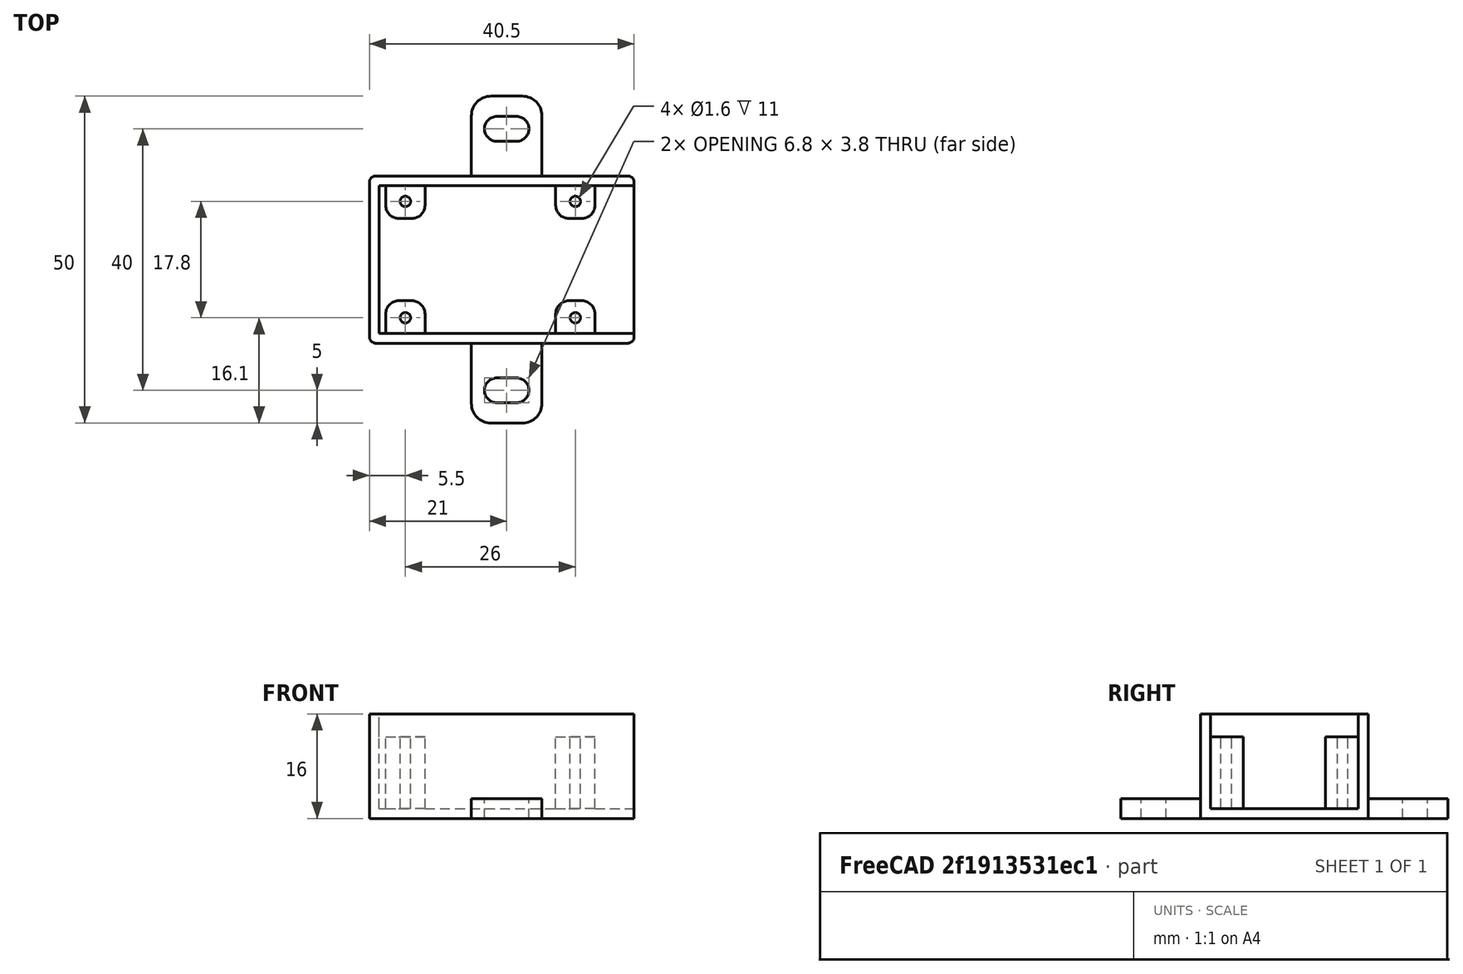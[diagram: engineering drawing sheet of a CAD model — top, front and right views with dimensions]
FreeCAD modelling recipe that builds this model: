
FCSTD DOCUMENT  (FreeCAD 0.18.4R)
Label: ds3231sn_clock
License: FreeArt
LicenseURL: http://artlibre.org/licence/lal
objects: Part::Box×4, Part::MultiFuse×4, Part::Fillet×2, Part::Cut×2, Spreadsheet::Sheet×1, Part::Cylinder×1, Part::FeaturePython×1, Part::Mirroring×1, Part::Feature×1, App::Part×1
note: 16 computed .brp shape members not serialized (recipe doc carries the construction recipe); baked Part::Feature solids carry a one-line shape summary decoded from their .brp

FEATURE [Spreadsheet::Sheet] Spreadsheet  label="p"
  cells = A1=pcb_x; B1(pcb_x)=39; A2=pcb_y; B2(pcb_y)=22.6; A3=pcb_z; B3(pcb_z)=1.5; A4=pcb_under; B4(pcb_under)=11; A5=side_wall; B5(side_wall)=1.5; A6=pcb_side_lane; B6(pcb_side_lane)=0; A7=bottom_wall; B7(bottom_wall)=1.5; A8=pcb_above; B8(pcb_above)=2; A9=hole_dist_x; B9(hole_dist_x)=26; A10=hole_dist_y; B10(hole_dist_y)=17.8; A11=hole_off_x; B11(hole_off_x)=4; A12=hole_r; B12(hole_r)=0.8; A13=hole_stand_x; B13(hole_stand_x)=6; A14=hole_stand_y; B14(hole_stand_y)=5
FEATURE [Part::Box] Box  label="external cube"
  AttacherType = Attacher::AttachEngine3D
  Height = 16
  Length = 40.5
  Width = 25.6
  expr: Height = p.bottom_wall + p.pcb_under + p.pcb_z + p.pcb_above
  expr: Width = p.pcb_y + 2 * p.side_wall
  expr: Length = p.pcb_x + p.side_wall
FEATURE [Part::Box] Box006  label="internal cube"
  AttacherType = Attacher::AttachEngine3D
  Height = 14.5
  Length = 40.5
  Placement = pos=(1.5,1.5,1.5) rot=(0,0,1;0rad)
  Width = 22.6
  expr: Placement.Base.y = p.side_wall + p.pcb_side_lane
  expr: Placement.Base.x = p.side_wall + p.pcb_side_lane
  expr: Placement.Base.z = p.bottom_wall
  expr: Height = p.pcb_under + p.pcb_z + p.pcb_above
  expr: Width = p.pcb_y - 2 * p.pcb_side_lane
  expr: Length = p.pcb_x - 2 * p.pcb_side_lane + p.side_wall
FEATURE [Part::Box] Box007  label="pcb extract cube"
  AttacherType = Attacher::AttachEngine3D
  Height = 1.5
  Length = 39
  Placement = pos=(1.5,1.5,12.5) rot=(0,0,1;0rad)
  Width = 22.6
  expr: Placement.Base.y = p.side_wall
  expr: Placement.Base.x = p.side_wall
  expr: Length = p.pcb_x
  expr: Width = p.pcb_y
  expr: Placement.Base.z = p.bottom_wall + p.pcb_under
  expr: Height = p.pcb_z
FEATURE [Part::MultiFuse] Fusion  label="extract fusion"
  Shapes = -> [Box006,Box007]
FEATURE [Part::Fillet] Fillet  label="external fillet"
  Base = -> Box
  Edges = 4 edges r=1: [Edge1,Edge3,Edge5,Edge7]
FEATURE [Part::Box] Box008  label="hole stand"
  AttacherType = Attacher::AttachEngine3D
  Height = 11
  Length = 6
  Placement = pos=(2.5,1.5,1.5) rot=(0,0,1;0rad)
  Width = 5
  expr: Placement.Base.x = p.side_wall + p.hole_off_x - p.hole_stand_x / 2
  expr: Placement.Base.y = p.side_wall
  expr: Length = p.hole_stand_x
  expr: Width = p.hole_stand_y
  expr: Placement.Base.z = p.bottom_wall
  expr: Height = p.pcb_under
FEATURE [Part::Cylinder] Cylinder  label="hole"
  Angle = 360
  AttacherType = Attacher::AttachEngine3D
  Height = 20
  Placement = pos=(5.5,3.9,0) rot=(0,0,1;0rad)
  Radius = 0.8
  expr: Placement.Base.y = p.side_wall + (p.pcb_y - p.hole_dist_y) / 2
  expr: Placement.Base.x = p.hole_off_x + p.side_wall
  expr: Radius = p.hole_r
FEATURE [Part::Fillet] Fillet001  label="hole stand fillet"
  Base = -> Box008
  Edges = 2 edges r=2: [Edge3,Edge7]
FEATURE [Part::Cut] Cut002003  label="hole cut"
  Base = -> Fillet001
  Tool = -> Cylinder
FEATURE [Part::FeaturePython] Array  label="hole cut array"  # Draft array (typed FeaturePython)
  Angle = 360
  ArrayType = 0
  Axis = (0,0,1)
  Base = -> Cut002003
  Center = (0,0,0)
  Fuse = false
  IntervalAxis = (0,0,0)
  IntervalX = (26,0,0)
  IntervalY = (0,1,0)
  IntervalZ = (0,0,1)
  NumberPolar = 1
  NumberX = 2
  NumberY = 0
  NumberZ = 1
  expr: IntervalX.x = p.hole_dist_x
FEATURE [Part::Mirroring] Part__Mirroring  label="hole stand (Mirror #1)"
  Base = (0,12.8,0)
  Normal = (0,1,0)
  Source = -> Array
  expr: Base.y = p.pcb_y / 2 + p.side_wall
FEATURE [Part::MultiFuse] Fusion002  label="hole fusion"
  Shapes = -> [Cut002003,Part__Mirroring,Array]
FEATURE [Part::Feature] Cut002001  label="attach plane y dir001"
  shape: bbox 10.8 x 50 x 3 mm, 18 faces (baked)
FEATURE [Part::MultiFuse] Fusion001  label="solid fusion"
  Shapes = -> [Fillet,Cut002001]
FEATURE [Part::Cut] Cut  label="sd card cut"
  Base = -> Fusion001
  Tool = -> Fusion
FEATURE [Part::MultiFuse] Fusion003  label="ds3231sn fusion"
  Shapes = -> [Fusion002,Cut]
FEATURE [App::Part] Part  label="ds3231sn pcb box part"
  Group = -> [Box,Fillet,Fusion001,Fusion,Box007,Box006,Cut,Part__Mirroring,Cut002003,Fusion002,Box008,Fillet001,Cylinder,Fusion003]
  Origin = -> Origin
